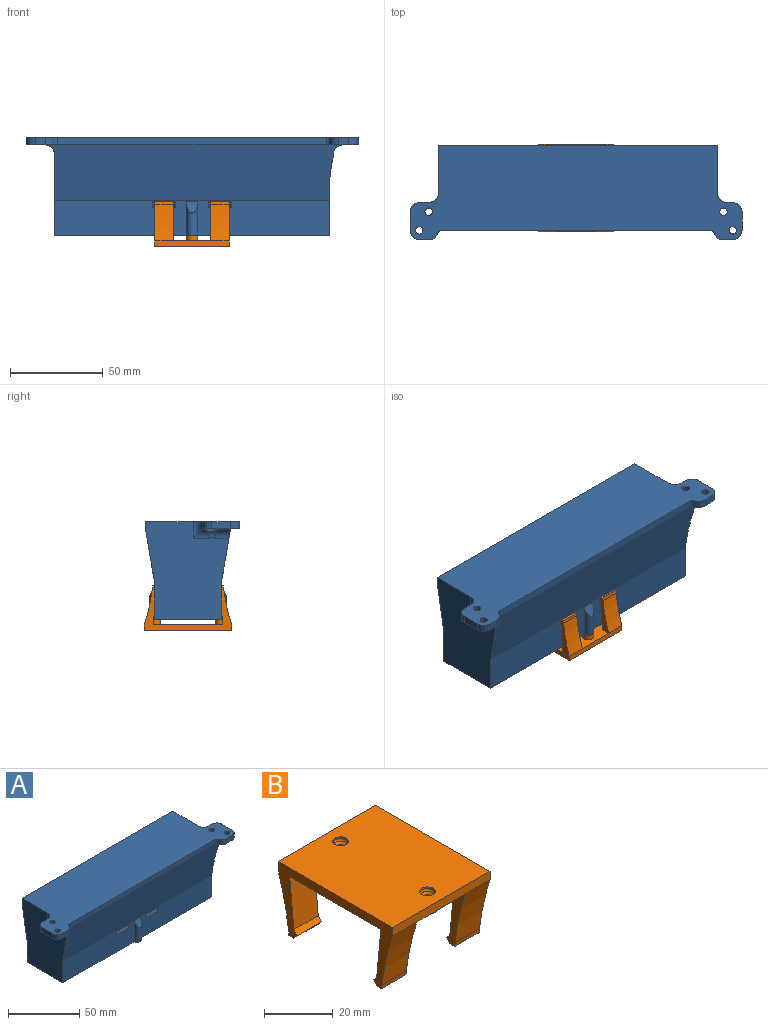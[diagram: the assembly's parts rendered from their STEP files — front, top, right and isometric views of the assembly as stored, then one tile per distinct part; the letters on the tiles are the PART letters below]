
ASSEMBLY  parts=2 mates=1
PART A: 74 faces, bbox 178.9x51x53 mm
  f0: plane 147.79x50.6mm, normal (0,1,0), area 7398.1mm2, adj f3,f13,f17,f19,f21,f22,f31,f73
  f1: plane 33.27x10mm, normal (1,0,0), area 260.7mm2, adj f6,f18,f31,f32,f58,f60,f62,f73
  f2: plane 6.84x1mm, normal (1,0,0), area 6.8mm2, adj f3,f5,f61,f73
  f3: cylinder r=65.43mm len=16.05mm, axis (0,-1,0), area 91.7mm2, adj f0,f2,f22,f61,f73
  f4: cylinder r=2mm len=4mm, axis (0,0,1), area 50.3mm2, adj f15,f18
  f5: cylinder r=5mm len=7.67mm, axis (0,1,0), area 52mm2, adj f2,f15,f61,f73
  f6: cylinder r=5mm len=7.67mm, axis (0,1,0), area 27.2mm2, adj f1,f15,f62,f73
  f7: cylinder r=5mm len=8.02mm, axis (0,-1,0), area 56.2mm2, adj f8,f10,f24,f61,f72
  f8: bspline ~5.05x5.04mm, area 15.1mm2, adj f7,f9,f24,f72
  f9: cylinder r=5mm len=8.02mm, axis (0,-1,0), area 34.4mm2, adj f8,f10,f24,f68,f72
  f10: plane 20x16.96mm, normal (0,0,-1), area 212.4mm2, adj f7,f9,f28,f29,f30,f33,f34,f61
  f11: plane 148x18.6mm, normal (0,-1,0), area 2572.8mm2, adj f12,f13,f22,f24,f40,f41,f42,f43
  f12: cylinder r=3mm len=18mm, axis (0,0,-1), area 133.6mm2, adj f11,f13,f52
  f13: plane 148x41.6mm, normal (0,0,-1), area 965.7mm2, adj f0,f11,f12,f14,f16,f20,f21,f22
  f14: cylinder r=3mm len=18mm, axis (0,0,-1), area 133.6mm2, adj f13,f23,f57
  f15: plane 20x16.96mm, normal (0,0,-1), area 198mm2, adj f4,f5,f6,f25,f26,f27,f35,f61
  f16: plane 26.55x4.32mm, normal (1,0,0), area 84.9mm2, adj f13,f20,f23,f32,f60
  f17: plane 146x29.6mm, normal (0,0,-1), area 4321.6mm2, adj f0,f19,f20,f21
  f18: plane 178.5x50.6mm, normal (0,0,1), area 7349.3mm2, adj f1,f4,f24,f25,f26,f27,f28,f29
  f19: plane 29.6x8mm, normal (-1,0,0), area 236.8mm2, adj f0,f17,f20,f31
  f20: plane 148x50.6mm, normal (0,-1,0), area 7398.2mm2, adj f13,f16,f17,f19,f21,f31,f32
  f21: plane 50.6x29.6mm, normal (1,0,0), area 1497.8mm2, adj f0,f13,f17,f20
  f22: plane 26.55x4.32mm, normal (1,0,0), area 84.9mm2, adj f0,f3,f11,f13,f61
  f23: plane 148x18.6mm, normal (0,1,0), area 2572.8mm2, adj f13,f14,f16,f24,f36,f37,f38,f39
  f24: plane 52.6x44.77mm, normal (-1,0,0), area 1885.1mm2, adj f7,f8,f9,f11,f13,f18,f23,f58
  f25: plane 5.25x4mm, normal (0,-1,0), area 21mm2, adj f15,f18,f63,f64
  f26: plane 10x4mm, normal (1,0,0), area 40mm2, adj f15,f18,f64,f65
  f27: plane 4x3.25mm, normal (0,1,0), area 13mm2, adj f15,f18,f62,f65
  f28: plane 10x4mm, normal (-1,0,0), area 40mm2, adj f10,f18,f66,f69
  f29: plane 5.25x4mm, normal (0,-1,0), area 21mm2, adj f10,f18,f66,f67
  f30: plane 5.25x4mm, normal (0,1,0), area 21mm2, adj f10,f18,f68,f69
  f31: plane 29.6x2mm, normal (0,0,-1), area 56.9mm2, adj f0,f1,f19,f20,f73
  f32: cylinder r=65.43mm len=16.05mm, axis (0,-1,0), area 91.8mm2, adj f1,f16,f20,f60
  f33: cylinder r=2mm len=4mm, axis (0,0,1), area 50.3mm2, adj f10,f18
  f34: cylinder r=2mm len=4mm, axis (0,0,1), area 50.3mm2, adj f10,f18
  f35: cylinder r=2mm len=4mm, axis (0,0,1), area 50.3mm2, adj f15,f18
  f36: plane 12x1.5mm, normal (0,0.86,-0.52), area 19.4mm2, adj f23,f37,f44,f45
  f37: plane 12x1.5mm, normal (0,0.86,0.52), area 19.4mm2, adj f23,f36,f44,f45
  f38: plane 12x1.5mm, normal (0,0.86,-0.52), area 19.4mm2, adj f23,f39,f46,f47
  f39: plane 12x1.5mm, normal (0,0.86,0.52), area 19.4mm2, adj f23,f38,f46,f47
  f40: plane 12x1.5mm, normal (0,-0.86,0.52), area 19.4mm2, adj f11,f41,f48,f49
  f41: plane 12x1.5mm, normal (0,-0.86,-0.52), area 19.4mm2, adj f11,f40,f48,f49
  f42: plane 12x1.5mm, normal (0,-0.86,0.52), area 19.4mm2, adj f11,f43,f50,f51
  f43: plane 12x1.5mm, normal (0,-0.86,-0.52), area 19.4mm2, adj f11,f42,f50,f51
  f44: plane 3x0.9mm, normal (-0.71,0.71,0), area 1.9mm2, adj f23,f36,f37
  f45: plane 3x0.9mm, normal (0.71,0.71,0), area 1.9mm2, adj f23,f36,f37
  f46: plane 3x0.9mm, normal (-0.71,0.71,0), area 1.9mm2, adj f23,f38,f39
  f47: plane 3x0.9mm, normal (0.71,0.71,0), area 1.9mm2, adj f23,f38,f39
  f48: plane 3x0.9mm, normal (0.71,-0.71,0), area 1.9mm2, adj f11,f40,f41
  f49: plane 3x0.9mm, normal (-0.71,-0.71,0), area 1.9mm2, adj f11,f40,f41
  f50: plane 3x0.9mm, normal (0.71,-0.71,0), area 1.9mm2, adj f11,f42,f43
  f51: plane 3x0.9mm, normal (-0.71,-0.71,0), area 1.9mm2, adj f11,f42,f43
  f52: plane 6x6mm, normal (0,-0.89,0.45), area 31.6mm2, adj f11,f12
  f53: cylinder r=1.25mm len=10mm, axis (0,0,-1), area 78.5mm2, adj f13,f54
  f54: plane 2.5x2.5mm, normal (0,0,-1), area 4.9mm2, adj f53
  f55: cylinder r=1.25mm len=10mm, axis (0,0,-1), area 78.5mm2, adj f13,f56
  f56: plane 2.5x2.5mm, normal (0,0,-1), area 4.9mm2, adj f55
  f57: plane 6x6mm, normal (0,0.89,0.45), area 31.6mm2, adj f14,f23
  f58: plane 150x4mm, normal (0,1,0), area 600mm2, adj f1,f18,f24,f60
  f59: plane 144.58x4mm, normal (0,-1,0), area 578.3mm2, adj f18,f61,f70,f71
  f60: plane 150.02x30.02mm, normal (0,0.99,-0.16), area 4524.2mm2, adj f1,f16,f23,f24,f32,f58
  f61: plane 160.35x30.35mm, normal (0,-0.99,-0.16), area 4535.1mm2, adj f2,f3,f5,f7,f10,f11,f15,f22
  f62: cylinder r=5mm len=9mm, axis (0,0,1), area 51.1mm2, adj f1,f6,f18,f27
  f63: cylinder r=5mm len=4.79mm, axis (0,0,1), area 25.6mm2, adj f15,f18,f25,f70
  f64: cylinder r=5mm len=5mm, axis (0,0,-1), area 31.4mm2, adj f15,f18,f25,f26
  f65: cylinder r=5mm len=5mm, axis (0,0,1), area 31.4mm2, adj f15,f18,f26,f27
  f66: cylinder r=5mm len=5mm, axis (0,0,1), area 31.4mm2, adj f10,f18,f28,f29
  f67: cylinder r=5mm len=4.79mm, axis (0,0,-1), area 25.6mm2, adj f10,f18,f29,f71
  f68: cylinder r=5mm len=9mm, axis (0,0,1), area 51.1mm2, adj f9,f18,f24,f30
  f69: cylinder r=5mm len=5mm, axis (0,0,-1), area 31.4mm2, adj f10,f18,f28,f30
  f70: cylinder r=2mm len=4mm, axis (0,0,1), area 10.2mm2, adj f15,f18,f59,f63
  f71: cylinder r=2mm len=4mm, axis (0,0,-1), area 10.2mm2, adj f10,f18,f59,f67
  f72: cylinder r=4mm len=7.98mm, axis (0,0,1), area 9.5mm2, adj f7,f8,f9,f10
  f73: cylinder r=4mm len=8mm, axis (0,0,1), area 43.8mm2, adj f0,f1,f2,f3,f5,f6,f15,f31
PART B: 46 faces, bbox 40x47x24 mm
  f0: plane 47x40mm, normal (0,0,-1), area 1631.6mm2, adj f1,f2,f3,f4,f5,f6,f8,f10
  f1: plane 18x10mm, normal (0,-1,0.09), area 180.8mm2, adj f0,f5,f6,f27
  f2: plane 18x10mm, normal (0,-1,0.09), area 180.8mm2, adj f0,f10,f11,f25
  f3: plane 18x10mm, normal (0,1,0.09), area 180.8mm2, adj f0,f11,f13,f24
  f4: plane 18x10mm, normal (0,1,0.09), area 180.8mm2, adj f0,f6,f8,f22
  f5: plane 21x7.82mm, normal (1,0,0), area 67.7mm2, adj f0,f1,f7,f27,f28,f29,f33
  f6: plane 47x24mm, normal (-1,0,0), area 276.5mm2, adj f0,f1,f4,f7,f9,f15,f16,f21
  f7: plane 10x2mm, normal (0,0,-1), area 20mm2, adj f5,f6,f28,f29
  f8: plane 21x7.82mm, normal (1,0,0), area 67.7mm2, adj f0,f4,f9,f21,f22,f31,f35
  f9: plane 10x2mm, normal (0,0,-1), area 20mm2, adj f6,f8,f21,f31
  f10: plane 21x7.82mm, normal (-1,0,0), area 67.7mm2, adj f0,f2,f12,f25,f26,f30,f34
  f11: plane 47x24mm, normal (1,0,0), area 276.5mm2, adj f0,f2,f3,f12,f14,f15,f16,f23
  f12: plane 10x2mm, normal (0,0,-1), area 20mm2, adj f10,f11,f26,f30
  f13: plane 21x7.82mm, normal (-1,0,0), area 67.7mm2, adj f0,f3,f14,f23,f24,f32,f36
  f14: plane 10x2mm, normal (0,0,-1), area 20mm2, adj f11,f13,f23,f32
  f15: plane 40x3mm, normal (0,-1,0), area 120mm2, adj f0,f6,f11,f35,f36,f39
  f16: plane 40x3mm, normal (0,1,0), area 120mm2, adj f0,f6,f11,f33,f34,f39
  f17: cylinder r=1.25mm len=4mm, axis (0,0,1), area 31.4mm2, adj f20,f45
  f18: cylinder r=1.25mm len=4mm, axis (0,0,1), area 31.4mm2, adj f19,f43
  f19: cone r=1.25mm half-angle=45deg, axis (0,0,1), area 10.1mm2, adj f18,f41
  f20: cone r=1.25mm half-angle=45deg, axis (0,0,1), area 10.1mm2, adj f17,f40
  f21: plane 10x1.5mm, normal (0,0.75,-0.66), area 20mm2, adj f6,f8,f9,f22
  f22: plane 10x1.5mm, normal (0,0.75,0.66), area 20mm2, adj f4,f6,f8,f21
  f23: plane 10x1.5mm, normal (0,0.75,-0.66), area 20mm2, adj f11,f13,f14,f24
  f24: plane 10x1.5mm, normal (0,0.75,0.66), area 20mm2, adj f3,f11,f13,f23
  f25: plane 10x1.5mm, normal (0,-0.75,0.66), area 20mm2, adj f2,f10,f11,f26
  f26: plane 10x1.5mm, normal (0,-0.75,-0.66), area 20mm2, adj f10,f11,f12,f25
  f27: plane 10x1.5mm, normal (0,-0.75,0.66), area 20mm2, adj f1,f5,f6,f28
  f28: plane 10x1.5mm, normal (0,-0.75,-0.66), area 20mm2, adj f5,f6,f7,f27
  f29: plane 10x1.54mm, normal (0,0.99,-0.12), area 15.5mm2, adj f5,f6,f7,f33
  f30: plane 10x1.54mm, normal (0,0.99,-0.12), area 15.5mm2, adj f10,f11,f12,f34
  f31: plane 10x1.54mm, normal (0,-0.99,-0.12), area 15.5mm2, adj f6,f8,f9,f35
  f32: plane 10x1.54mm, normal (0,-0.99,-0.12), area 15.5mm2, adj f11,f13,f14,f36
  f33: cylinder r=100mm len=19.46mm, axis (1,0,0), area 199.6mm2, adj f5,f6,f16,f29
  f34: cylinder r=100mm len=19.46mm, axis (1,0,0), area 199.6mm2, adj f10,f11,f16,f30
  f35: cylinder r=100mm len=19.46mm, axis (1,0,0), area 199.6mm2, adj f6,f8,f15,f31
  f36: cylinder r=100mm len=19.46mm, axis (1,0,0), area 199.6mm2, adj f11,f13,f15,f32
  f37: cylinder r=2.25mm len=4.5mm, axis (0,0,-1), area 8.3mm2, adj f39,f40
  f38: cylinder r=2.25mm len=4.5mm, axis (0,0,-1), area 8.3mm2, adj f39,f41
  f39: plane 47x40mm, normal (0,0,1), area 1848.2mm2, adj f6,f11,f15,f16,f37,f38
  f40: torus R=1.25mm, axis (0,0,-1), area 10.6mm2, adj f20,f37
  f41: torus R=1.25mm, axis (0,0,-1), area 10.6mm2, adj f19,f38
  f42: cylinder r=3mm len=6mm, axis (0,0,1), area 56.5mm2, adj f0,f43
  f43: plane 6x6mm, normal (0,0,-1), area 23.4mm2, adj f18,f42
  f44: cylinder r=3mm len=6mm, axis (0,0,1), area 56.5mm2, adj f0,f45
  f45: plane 6x6mm, normal (0,0,-1), area 23.4mm2, adj f17,f44
PLACE A t=(31,0,0)mm
PLACE B rot(axis=(0,1,0),180deg) t=(31,17.8,-57.6)mm
MATE fastened B.f17 <-> A.f14  axis (0,0,1) through (31,35.6,-52.6)mm
